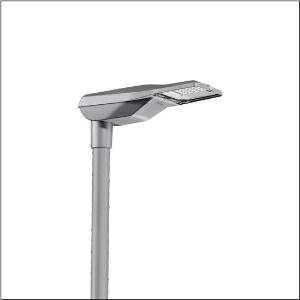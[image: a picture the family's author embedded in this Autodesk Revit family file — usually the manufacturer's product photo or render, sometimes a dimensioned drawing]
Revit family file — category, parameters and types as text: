
# Revit family: streetlight_sl_21_iq_micro___p0_5a_5xe1v31d08db_e47d
name_source: partatom
category: Lighting Fixtures
units: mm (PartAtom-declared; Revit-internal decimal feet)

## family parameters
Cut with Voids When Loaded = No
Host = Face
Light Source = No
Part Type = Normal
Room Calculation Point = No
Round Connector Dimension = Use Diameter
Shared = No

## types (1)
- --- (1 x LED, 4660 lm, 36.4 W, 3000K)
    Apparent Load = 36 VA
    CIE Flux Codes = 37 73 96 100 100
    Color Rendering = 70
    Color Temperature = 3000K
    Default Elevation = 1800 mm
    Description = Streetlight SL 21 iQ micro, mast luminaire, primary light control with lens, of PMMA, primary optical cover: cover, of toughened safety glass, transparent, light distribution: P0.5a, light emission: direct distribution, primary light characteristic: asymmetric, installation type: post-top, side-entry, LED, High Power LED, rated luminous flux: 4.660lm, luminous efficacy: 128lm/W, light colour: 730, colour temperature: 3000K, control gear: iQ-Comfort, control: pre-setting: linear dimming characteristic, Auto-Match, Temp-Guard, Lumen-Switch, Night-Set, Smart-Wire, Light-Fading, Desk-Remote (wireless, voltage-free reading and setting of iQ features in the workshop via application-optimized NFC function/RFID function), optimised constant luminous flux control (CLO 2.0), mains connection: 220..240V, AC, 50/60Hz, start of lifetime: 36W, end of service life: 38W, reduction: 16W, luminaire housing, of diecast aluminium, powder-coated, Siteco® metallic grey (DB 702S), corrosivity category C5 high according to DIN EN ISO 12944, please order mast flange separately, inclination adjustable: 0°, 5°, 10°, 15°, sealing non-destructively replaceable, multi-level sealing system, length: 528mm, width: 235mm, height: 110mm, mast flange for spigot size: 42mm (side-entry): 5XC10008XM4, 60/48mm (side-entry/post-top): 5XC10108XM2, 76/60mm (side-entry/post-top): 5XC10108XM1, protection rating (complete): IP66, insulation class (complete): insulation class II (safety insulation), certification: CE, ENEC, ENEC+, VDE, impact resistance: IK10, permissible operating ambient temperature for outdoor applications: -40..+50°C, standard-compliant lighting for roads and squares, packaging unit: 1 piece

Light Distribution: P0.5a
    Height = 110 mm
    Lamp = 1 x LED
    Lamp Light Flux = 4660 lm
    Lamp Power = 36.4 W
    Lamp count = 1
    Length = 528 mm
    Luminous efficacy = 128 lm/W
    Manufacturer = Siteco
    ModVariant = No
    Model = 5XE1V31D08DB
    Number of Poles = 1
    OnlyDefault = Yes
    Power Factor = 1
    Product Name = Streetlight SL 21 iQ micro | P0.5a
    Product group = mast luminaire | pylon top
    ProductGroupID = 6100
    Protection Class = Protection class II
    Protection Degree = IP 66
    RLX_Detail_Level = 1
    RLX_Emergency_Light_Flux = 0 lm
    RLX_Emergency_Type = 0
    RLX_Emergency_Type_DB = No
    RlxData = <blob elided: 98405 chars, md5=7c72c05b>
    Socket = socket
    Standby Power = 0 W
    System Light Flux = 4660 lm
    System Power = 36 W
    Type Comments = factory setting: luminous flux: 100 % | dim-lin: 254 | 715 mA
    Type Image = l_1006881.jpg
    URL = http://relux.com
    VarID = @adj_080823
    Voltage = 0 V
    Weight = 0.00 kg
    Width = 235 mm

## geometry (parser evidence)
native form markers: Blend x4, Sweep x11
no freeform markers — native parametric forms only
